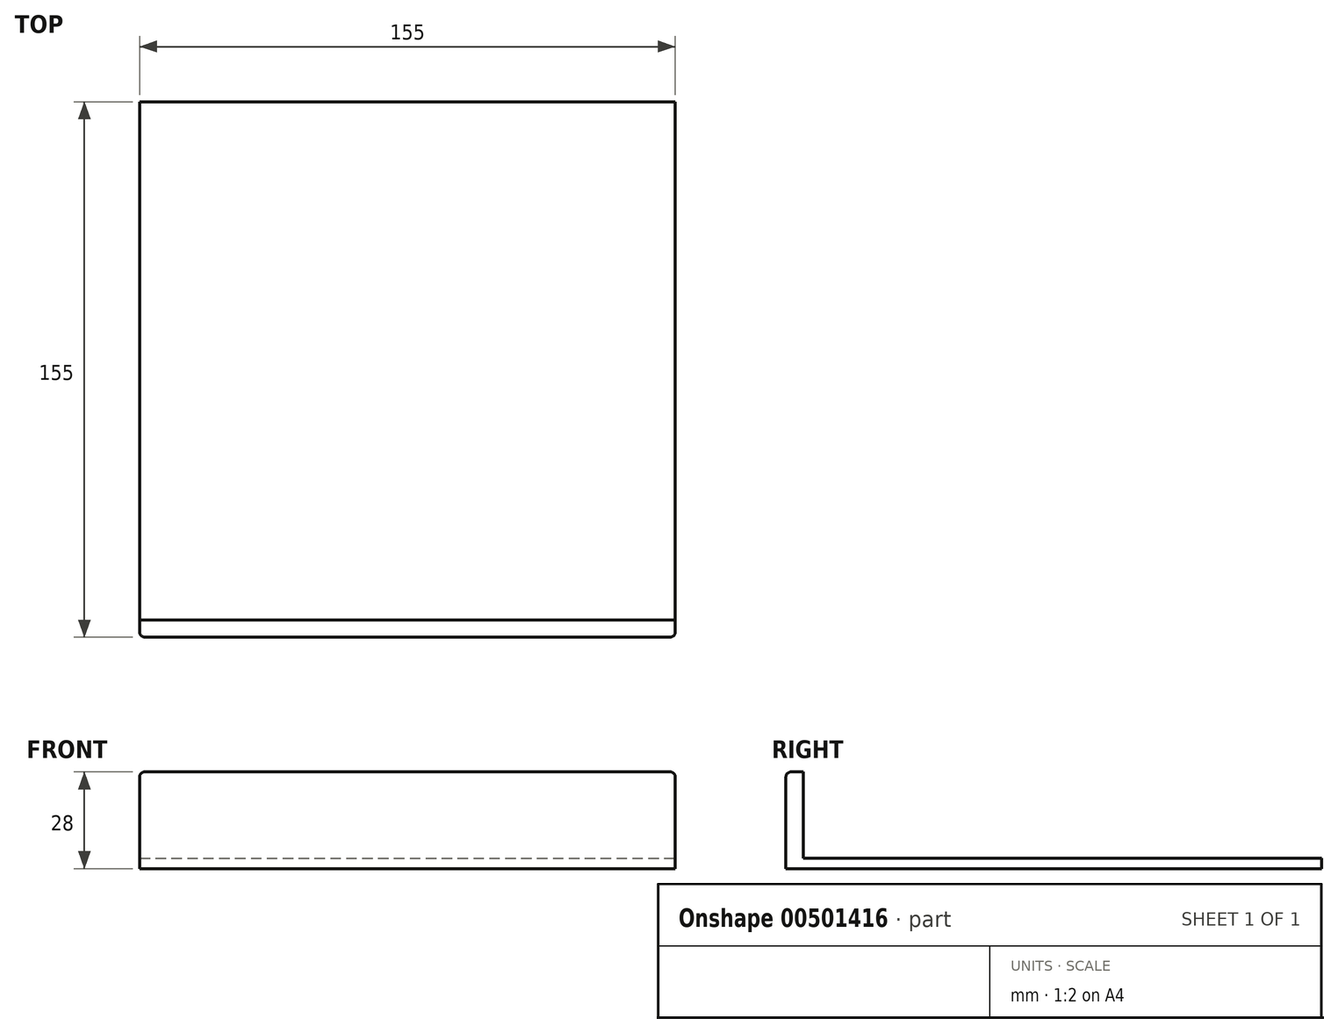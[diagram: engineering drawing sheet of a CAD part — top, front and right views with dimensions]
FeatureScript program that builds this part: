
annotation { "Feature Type Name" : "Feature", "Feature Type Description" : "" }
export const myFeature = defineFeature(function(context is Context, id is Id, definition is map)
    precondition{}
    {
        {
            var Q0;
            Q0=qCreatedBy(makeId("Top.planeOp"),FACE);
            var sketch = newSketch(context, id + "F0", { "sketchPlane" : qUnion([Q0])});
            skLineSegment(sketch, "E0.bottom", {"start": v(0, 0) * mm, "end": v(155, 0) * mm});
            skLineSegment(sketch, "E0.top", {"start": v(0, 155) * mm, "end": v(155, 155) * mm});
            skLineSegment(sketch, "E0.left", {"start": v(0, 0) * mm, "end": v(0, 155) * mm});
            skLineSegment(sketch, "E0.right", {"start": v(155, 0) * mm, "end": v(155, 155) * mm});
            skLineSegment(sketch, "E1", {"start": v(0, 5) * mm, "end": v(155, 5) * mm});
            skSolve(sketch);
        }
        {
            var Q0;
            {var subQ0=sQuery(id+"F0.wireOp",EDGE,"E0.bottom");Q0=makeQuery(id+"F0.imprint","IMPRINT",FACE,{"disambiguationData":[TD([[makeQuery(id+"F0.imprint","IMPRINT",EDGE,{"derivedFrom":subQ0}),1.0]])]});}
            extrude(context, id + "F1", {"entities" : qUnion([Q0]), "depth" : 28 * mm});
        }
        {
            var Q0;
            Q0 = qSketchRegion(id + "F0", true);
            extrude(context, id + "F2", {"entities" : qUnion([Q0]), "operationType" : NewBodyOperationType.ADD, "depth" : 3 * mm});
        }
        {
            var Q0;
            Q0=makeQuery(id+"F1.opExtrude","CAP_EDGE",EDGE,{"disambiguationData":[OSD([sQuery(id+"F0.wireOp",EDGE,"E0.bottom")])],"isStart":false});
            fillet(context, id + "F3", {"entities" : qUnion([Q0]), "radius" : 1.5 * mm, "tangentPropagation" : true, "allowEdgeOverflow" : false});
        }
        {
            var Q0;
            Q0=makeQuery(id+"F1.opExtrude","SWEPT_EDGE",EDGE,{"disambiguationData":[OSD([sQuery(id+"F0.wireOp",EDGE,"E0.bottom"),sQuery(id+"F0.wireOp",EDGE,"E0.left")])]});
            var Q1;
            Q1=makeQuery(id+"F1.opExtrude","SWEPT_EDGE",EDGE,{"disambiguationData":[OSD([sQuery(id+"F0.wireOp",EDGE,"E0.bottom"),sQuery(id+"F0.wireOp",EDGE,"E0.right")])]});
            fillet(context, id + "F4", {"entities" : qUnion([Q0, Q1]), "radius" : 1.5 * mm, "tangentPropagation" : true, "allowEdgeOverflow" : false});
        }
    });
